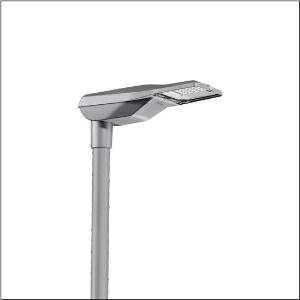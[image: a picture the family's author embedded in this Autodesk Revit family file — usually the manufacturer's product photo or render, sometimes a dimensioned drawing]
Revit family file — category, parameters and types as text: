
# Revit family: streetlight_sl_21_iq_micro___st1_5a_5xe1p41d08cb_4bae
name_source: partatom
category: Lighting Fixtures
units: mm (PartAtom-declared; Revit-internal decimal feet)

## family parameters
Cut with Voids When Loaded = No
Host = Face
Light Source = No
Part Type = Normal
Room Calculation Point = No
Round Connector Dimension = Use Diameter
Shared = No

## types (1)
- --- (1 x LED, 2930 lm, 19.4 W, 4000K)
    Apparent Load = 19 VA
    CIE Flux Codes = 22 53 95 100 100
    Color Rendering = 70
    Color Temperature = 4000K
    Default Elevation = 1800 mm
    Description = Streetlight SL 21 iQ micro, mast luminaire, primary light control with lens, of PMMA, primary optical cover: cover, of toughened safety glass, transparent, light distribution: ST1.5a, light emission: direct distribution, primary light characteristic: asymmetric, installation type: post-top, side-entry, LED, High Power LED, rated luminous flux: 2.930lm, luminous efficacy: 151lm/W, light colour: 740, colour temperature: 4000K, control: Auto-Match, Temp-Guard, Lumen-Switch, Night-Set, Smart-Wire, Light-Fading, Desk-Remote (wireless, voltage-free reading and setting of iQ features in the workshop via application-optimized NFC function/RFID function), optimised constant luminous flux control (CLO 2.0), pre-setting: linear dimming characteristic, mains connection: 220..240V, AC, 50/60Hz, start of lifetime: 19W, end of service life: 20W, reduction: 10W, luminaire housing, of diecast aluminium, powder-coated, Siteco® metallic grey (DB 702S), corrosivity category C5 mid according to DIN EN ISO 12944, please order mast flange separately, inclination adjustable: 0°, 5°, 10°, 15°, sealing non-destructively replaceable, multi-level sealing system, length: 528mm, width: 235mm, height: 110mm, mast flange for spigot size: 42mm (side-entry): 5XC10008XM4, 60/48mm (side-entry/post-top): 5XC10108XM2, 76/60mm (side-entry/post-top): 5XC10108XM1, protection rating (complete): IP66, insulation class (complete): insulation class II (safety insulation), certification: CE, ENEC, ENEC+, VDE, impact resistance: IK09, permissible operating ambient temperature for outdoor applications: -40..+50°C, standard-compliant lighting for roads and squares, packaging unit: 1 piece

Light Distribution: ST1.5a
    Height = 110 mm
    Lamp = 1 x LED
    Lamp Light Flux = 2930 lm
    Lamp Power = 19.4 W
    Lamp count = 1
    Length = 528 mm
    Luminous efficacy = 151 lm/W
    Manufacturer = Siteco
    ModVariant = No
    Model = 5XE1P41D08CB
    Number of Poles = 1
    OnlyDefault = Yes
    Power Factor = 1
    Product Name = Streetlight SL 21 iQ micro | ST1.5a
    Product group = mast luminaire | pylon top
    ProductGroupID = 6100
    Protection Class = Protection class II
    Protection Degree = IP 66
    RLX_Detail_Level = 1
    RLX_Emergency_Light_Flux = 0 lm
    RLX_Emergency_Type = 0
    RLX_Emergency_Type_DB = No
    RlxData = <blob elided: 103585 chars, md5=c040ff80>
    Socket = socket
    Standby Power = 0 W
    System Light Flux = 2930 lm
    System Power = 19 W
    Type Comments = factory setting: luminous flux: 100 % | dim-lin: 254 | 387 mA
    Type Image = l_1006881.jpg
    URL = http://relux.com
    VarID = @adj_107839
    Voltage = 0 V
    Weight = 0.00 kg
    Width = 235 mm

## geometry (parser evidence)
native form markers: Blend x4, Sweep x9
no freeform markers — native parametric forms only
